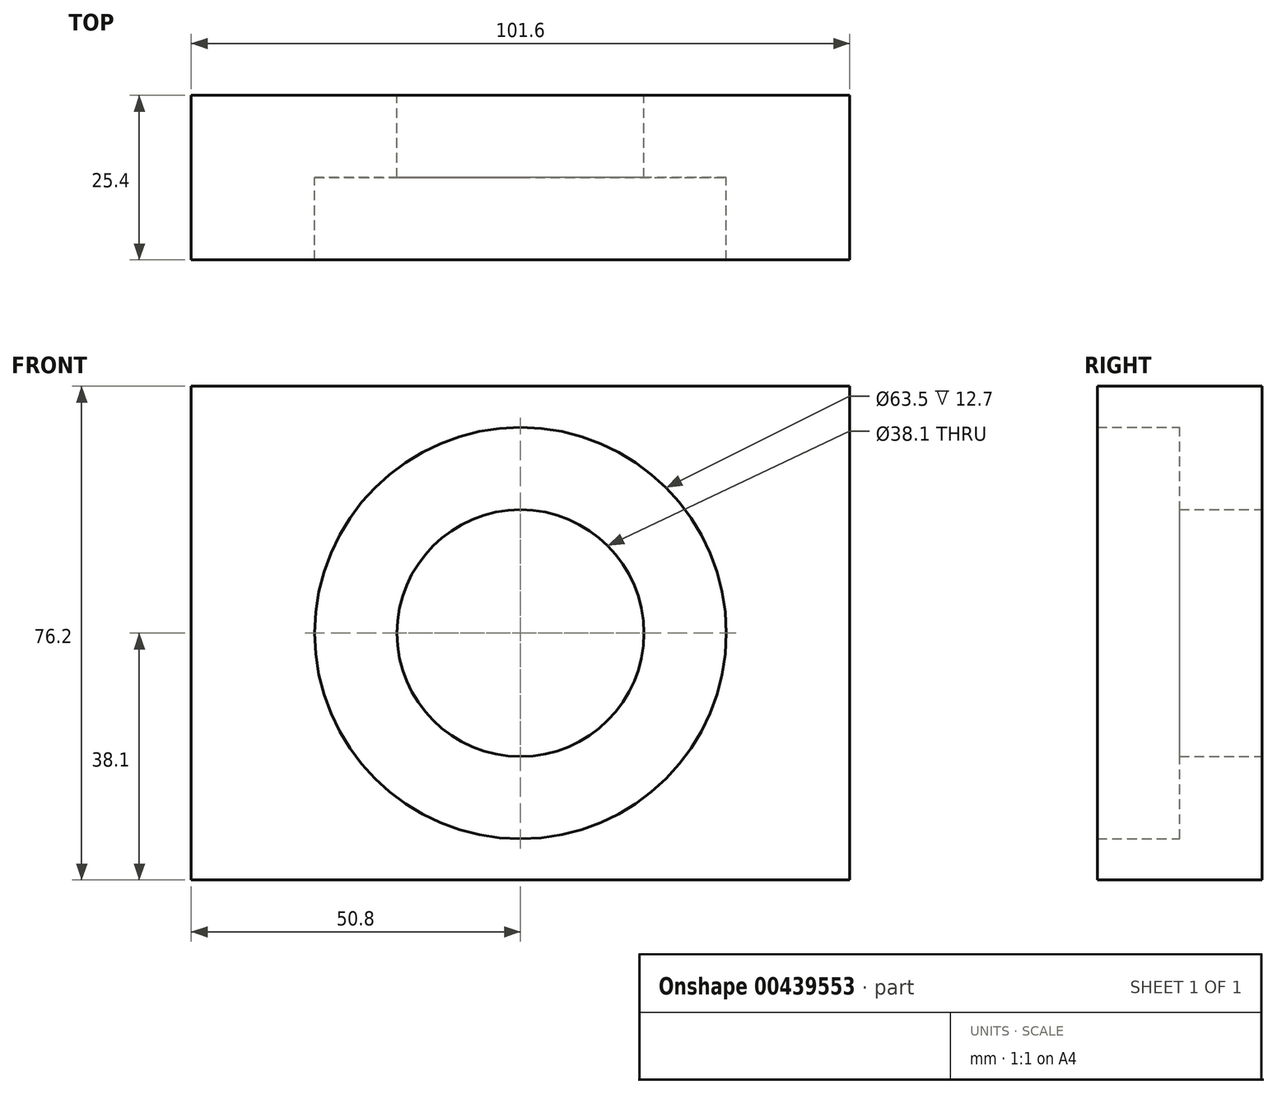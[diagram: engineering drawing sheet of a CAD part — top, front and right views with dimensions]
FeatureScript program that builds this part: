
annotation { "Feature Type Name" : "Feature", "Feature Type Description" : "" }
export const myFeature = defineFeature(function(context is Context, id is Id, definition is map)
    precondition{}
    {
        {
            var Q0;
            Q0=qCreatedBy(makeId("Front.planeOp"),FACE);
            var sketch = newSketch(context, id + "F0", { "sketchPlane" : qUnion([Q0])});
            skLineSegment(sketch, "E0.bottom", {"start": v(0, 76.2) * mm, "end": v(101.6, 76.2) * mm});
            skLineSegment(sketch, "E0.top", {"start": v(0, 0) * mm, "end": v(101.6, 0) * mm});
            skLineSegment(sketch, "E0.left", {"start": v(0, 76.2) * mm, "end": v(0, 0) * mm});
            skLineSegment(sketch, "E0.right", {"start": v(101.6, 76.2) * mm, "end": v(101.6, 0) * mm});
            skCircle(sketch, "E1", {"center": v(50.8, 38.1) * mm, "radius": 19.05 * mm});
            skPoint(sketch, "E1.centerSnap0", {"position": v(101.6, 38.1) * mm});
            skPoint(sketch, "E1.centerSnap1", {"position": v(50.8, 76.2) * mm});
            skCircle(sketch, "E2", {"center": v(50.8, 38.1) * mm, "radius": 31.75 * mm});
            skSolve(sketch);
        }
        {
            var Q0;
            Q0=makeQuery(id+"F0.imprint","IMPRINT",FACE,{"disambiguationData":[TD([[makeQuery(id+"F0.imprint","IMPRINT",EDGE,{"derivedFrom":sQuery(id+"F0.wireOp",EDGE,"E0.bottom")}),-1.0]])]});
            extrude(context, id + "F1", {"entities" : qUnion([Q0]), "depth" : 25.4 * mm});
        }
        {
            var Q0;
            Q0=makeQuery(id+"F0.imprint","IMPRINT",FACE,{"disambiguationData":[TD([[makeQuery(id+"F0.imprint","IMPRINT",EDGE,{"derivedFrom":sQuery(id+"F0.wireOp",EDGE,"E1")}),-1.0]])]});
            extrude(context, id + "F2", {"entities" : qUnion([Q0]), "operationType" : NewBodyOperationType.ADD, "depth" : 12.7 * mm});
        }
    });
